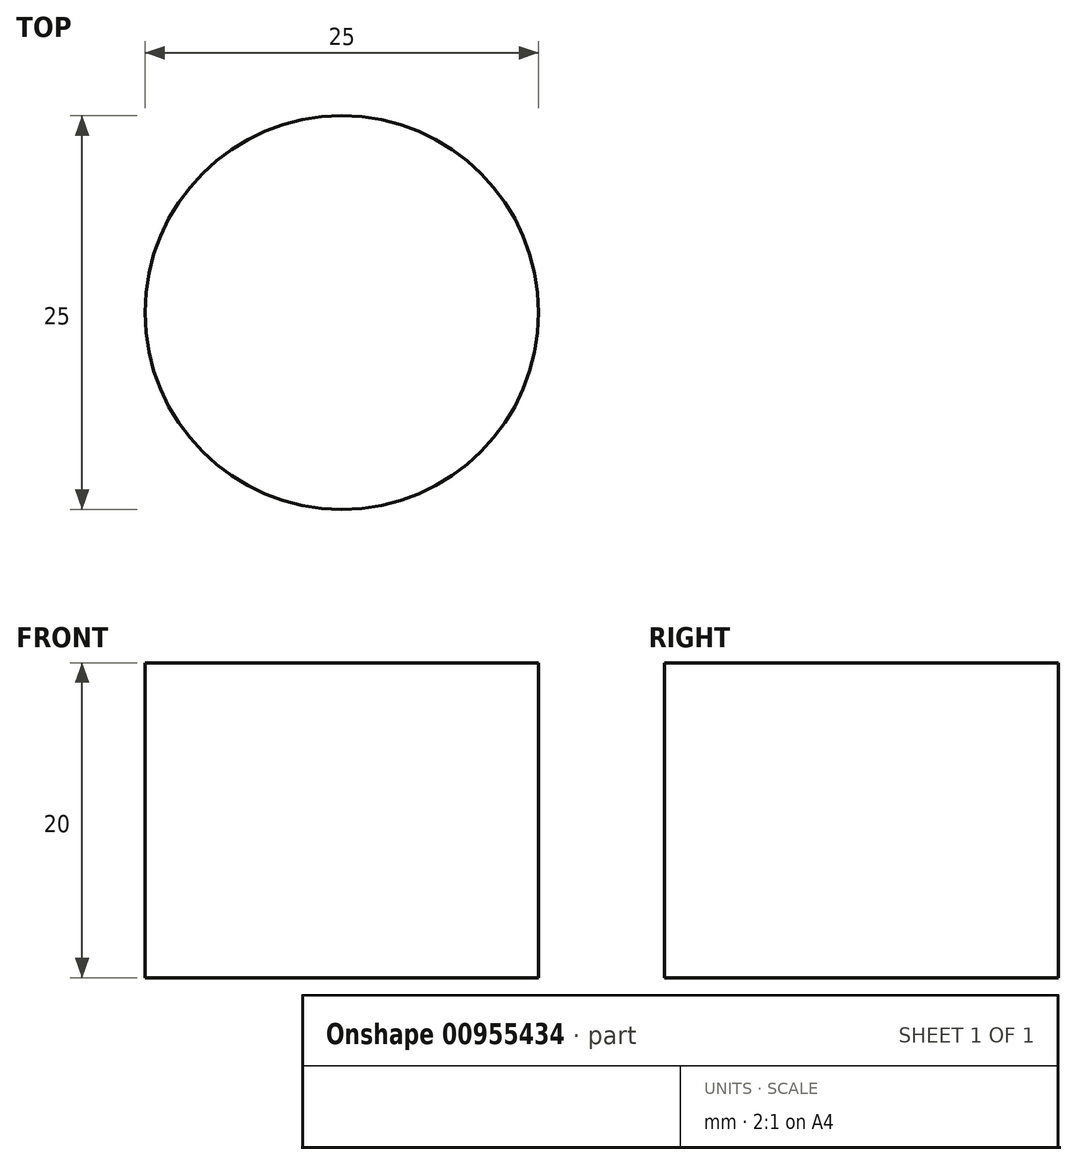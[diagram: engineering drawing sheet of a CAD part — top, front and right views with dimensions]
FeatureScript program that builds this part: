
annotation { "Feature Type Name" : "Feature", "Feature Type Description" : "" }
export const myFeature = defineFeature(function(context is Context, id is Id, definition is map)
    precondition{}
    {
        {
            var Q0;
            Q0=qCreatedBy(makeId("Top.planeOp"),FACE);
            var sketch = newSketch(context, id + "F0", { "sketchPlane" : qUnion([Q0])});
            skCircle(sketch, "E0", {"center": v(0, 0) * mm, "radius": 12.5 * mm});
            skSolve(sketch);
        }
        {
            var Q0;
            Q0 = qSketchRegion(id + "F0", true);
            extrude(context, id + "F1", {"entities" : qUnion([Q0]), "depth" : 20 * mm, "offsetDistance" : 25 * mm});
        }
    });
